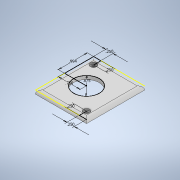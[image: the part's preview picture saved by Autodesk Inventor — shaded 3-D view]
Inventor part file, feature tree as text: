
AUTODESK INVENTOR PART (.ipt)
format: ipt  version: 2020 (Build 240168000, 168)  size: 131,584 bytes
history: native  units: in
note: dims shown in document units (in); Inventor stores cm internally (conversion verified against a paired STEP export)
features: extrude x2, sketch x2, hole x1, fillet x1
ambient origin geometry x8: Origin, YZ Plane, XZ Plane, XY Plane, X Axis, Y Axis, Z Axis, Center Point
bodies: Solid1 (feature_tree)
feature tree (6):
  extrude  "Extrusion1"  Depth=1.988in
  sketch  "Sketch2"  dims[d2=0.125in d3=0.0in d4=0.25in d5=0.25in d6=0.25in d7=0.25in d8=0.129in d9=0.75in d10=0.219in d11=0.0625in d12=0.5635in d13=0.5in d14=0.8108in d15=0.994in d16=0.75in d17=0.875in d18=0.125in d19=0.0in d20=0.125in]
  hole  "Hole1"  [1 undecoded]
  extrude  "Extrusion2"  Depth=0.125in
  fillet  "Fillet1"  Radius=0.25in
  sketch  "Sketch1"  dims[d0=1.75in d1=1.988in]
note: 1 required parameter value undecoded (feature->parameter linkage not recoverable at this tier; creation-order binding heuristic only, values carry confidence <= 0.55)
